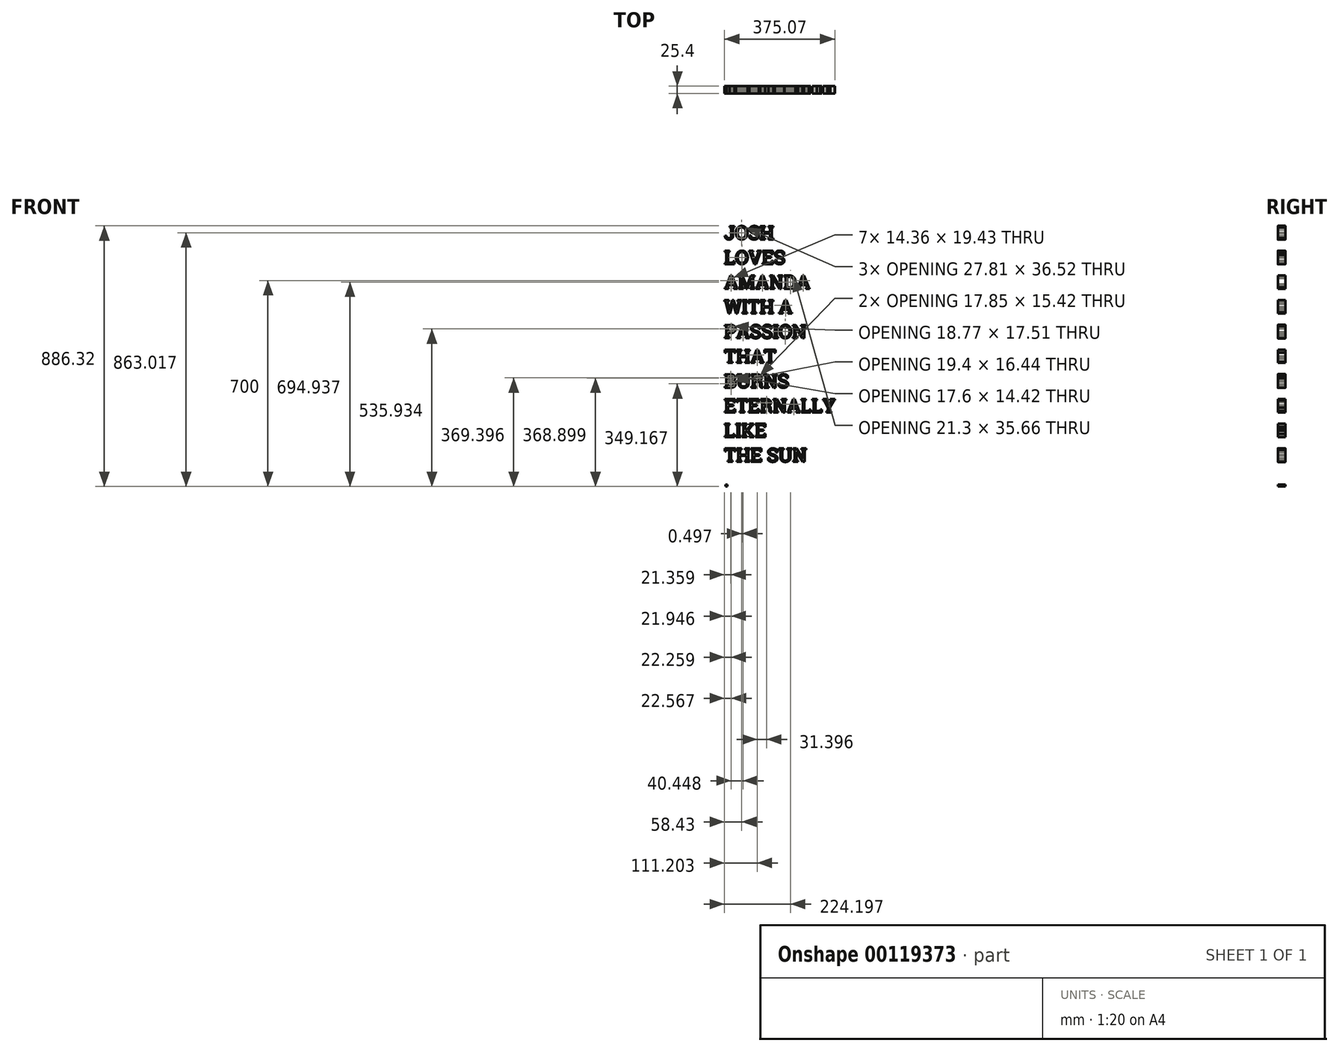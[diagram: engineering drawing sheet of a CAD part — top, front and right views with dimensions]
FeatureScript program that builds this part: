
annotation { "Feature Type Name" : "Feature", "Feature Type Description" : "" }
export const myFeature = defineFeature(function(context is Context, id is Id, definition is map)
    precondition{}
    {
        {
            var Q0;
            Q0=qCreatedBy(makeId("Front.planeOp"),FACE);
            var sketch = newSketch(context, id + "F0", { "sketchPlane" : qUnion([Q0])});
            skText(sketch, "E0", { "text": "JOSH \nLOVES\nAMANDA\nWITH A \nPASSION\nTHAT\nBURNS \nETERNALLY\nLIKE \nTHE SUN\n.", "fontName": "RobotoSlab-Regular.ttf"});
            const initialGuessF0  = {"E0": [-0.06972, -0.0171, 1, 0, 0.04584]};
            skSetInitialGuess(sketch, initialGuessF0);
            skSolve(sketch);
        }
        {
            var Q0;
            Q0 = qSketchRegion(id + "F0", true);
            extrude(context, id + "F1", {"entities" : qUnion([Q0]), "depth" : 25.4 * mm});
        }
    });
